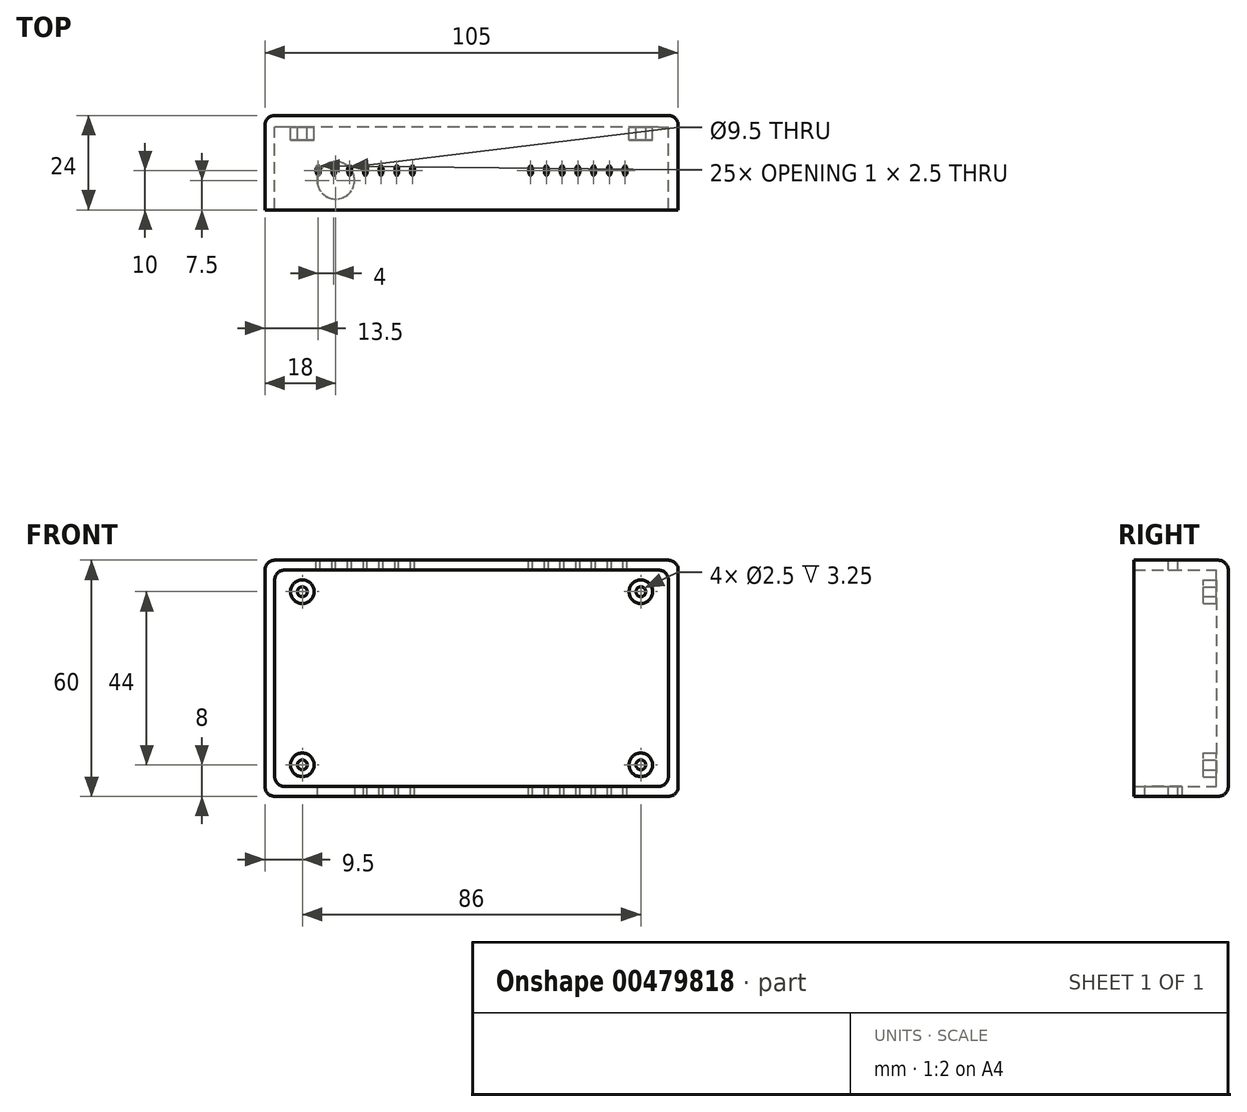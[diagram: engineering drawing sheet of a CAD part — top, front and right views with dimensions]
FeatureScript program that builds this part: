
annotation { "Feature Type Name" : "Feature", "Feature Type Description" : "" }
export const myFeature = defineFeature(function(context is Context, id is Id, definition is map)
    precondition{}
    {
        {
            var Q0;
            Q0=qCreatedBy(makeId("Front.planeOp"),FACE);
            var sketch = newSketch(context, id + "F0", { "sketchPlane" : qUnion([Q0])});
            skLineSegment(sketch, "E0.bottom", {"start": v(50, 27.5) * mm, "end": v(-50, 27.5) * mm});
            skLineSegment(sketch, "E0.top", {"start": v(50, -27.5) * mm, "end": v(-50, -27.5) * mm});
            skLineSegment(sketch, "E0.left", {"start": v(50, 27.5) * mm, "end": v(50, -27.5) * mm});
            skLineSegment(sketch, "E0.right", {"start": v(-50, 27.5) * mm, "end": v(-50, -27.5) * mm});
            skPoint(sketch, "E0.middle", {"position": v(0, 0) * mm});
            skLineSegment(sketch, "E1.bottom", {"start": v(-52.5, 30) * mm, "end": v(52.5, 30) * mm});
            skLineSegment(sketch, "E1.top", {"start": v(-52.5, -30) * mm, "end": v(52.5, -30) * mm});
            skLineSegment(sketch, "E1.left", {"start": v(-52.5, 30) * mm, "end": v(-52.5, -30) * mm});
            skLineSegment(sketch, "E1.right", {"start": v(52.5, 30) * mm, "end": v(52.5, -30) * mm});
            skSolve(sketch);
        }
        {
            var Q0;
            Q0=makeQuery(id+"F0.imprint","IMPRINT",FACE,{"disambiguationData":[TD([[makeQuery(id+"F0.imprint","IMPRINT",EDGE,{"derivedFrom":sQuery(id+"F0.wireOp",EDGE,"E0.bottom")}),1.0]])]});
            var sketch = newSketch(context, id + "F1", { "sketchPlane" : qUnion([Q0])});
            skLineSegment(sketch, "E2.bottom", {"start": v(-43, -22) * mm, "end": v(43, -22) * mm, "construction": true});
            skLineSegment(sketch, "E2.top", {"start": v(-43, 22) * mm, "end": v(43, 22) * mm, "construction": true});
            skLineSegment(sketch, "E2.left", {"start": v(-43, -22) * mm, "end": v(-43, 22) * mm, "construction": true});
            skLineSegment(sketch, "E2.right", {"start": v(43, -22) * mm, "end": v(43, 22) * mm, "construction": true});
            skPoint(sketch, "E2.middle", {"position": v(0, 0) * mm});
            skCircle(sketch, "E3", {"center": v(-43, 22) * mm, "radius": 1.25 * mm});
            skCircle(sketch, "E4", {"center": v(-43, 22) * mm, "radius": 3 * mm});
            skCircle(sketch, "E5", {"center": v(-43, -22) * mm, "radius": 1.25 * mm});
            skCircle(sketch, "E6", {"center": v(-43, -22) * mm, "radius": 3 * mm});
            skCircle(sketch, "E7", {"center": v(43, -22) * mm, "radius": 1.25 * mm});
            skCircle(sketch, "E8", {"center": v(43, -22) * mm, "radius": 3 * mm});
            skCircle(sketch, "E9", {"center": v(43, 22) * mm, "radius": 1.25 * mm});
            skCircle(sketch, "E10", {"center": v(43, 22) * mm, "radius": 3 * mm});
            skLineSegment(sketch, "E11.bottom", {"start": v(-43, -22) * mm, "end": v(-34.5, -22) * mm, "construction": true});
            skLineSegment(sketch, "E11.top", {"start": v(-43, -31.16) * mm, "end": v(-34.5, -31.16) * mm, "construction": true});
            skLineSegment(sketch, "E11.left", {"start": v(-43, -22) * mm, "end": v(-43, -31.16) * mm, "construction": true});
            skLineSegment(sketch, "E11.right", {"start": v(-34.5, -22) * mm, "end": v(-34.5, -31.16) * mm, "construction": true});
            skSolve(sketch);
        }
        {
            var Q0;
            Q0=makeQuery(id+"F0.imprint","IMPRINT",FACE,{"disambiguationData":[TD([[makeQuery(id+"F0.imprint","IMPRINT",EDGE,{"derivedFrom":sQuery(id+"F0.wireOp",EDGE,"E0.bottom")}),-1.0]])]});
            extrude(context, id + "F2", {"entities" : qUnion([Q0]), "depth" : 24 * mm});
        }
        {
            var Q0;
            Q0=makeQuery(id+"F0.imprint","IMPRINT",FACE,{"disambiguationData":[TD([[makeQuery(id+"F0.imprint","IMPRINT",EDGE,{"derivedFrom":sQuery(id+"F0.wireOp",EDGE,"E0.bottom")}),1.0]])]});
            var Q1;
            Q1=makeQuery(id+"F1.imprint","IMPRINT",FACE,{"disambiguationData":[TD([[makeQuery(id+"F1.imprint","IMPRINT",EDGE,{"derivedFrom":sQuery(id+"F1.wireOp",EDGE,"E9")}),-1.0]])]});
            var Q2;
            Q2=makeQuery(id+"F1.imprint","IMPRINT",FACE,{"disambiguationData":[TD([[makeQuery(id+"F1.imprint","IMPRINT",EDGE,{"derivedFrom":sQuery(id+"F1.wireOp",EDGE,"E4")}),-1.0]])]});
            extrude(context, id + "F3", {"entities" : qUnion([Q0, Q1, Q2]), "operationType" : NewBodyOperationType.ADD, "depth" : 3 * mm});
        }
        {
            var Q0;
            Q0=makeQuery(id+"F2.opExtrude","CAP_EDGE",EDGE,{"disambiguationData":[OSD([sQuery(id+"F0.wireOp",EDGE,"E1.top")])],"isStart":true});
            var Q1;
            Q1=makeQuery(id+"F2.opExtrude","CAP_EDGE",EDGE,{"disambiguationData":[OSD([sQuery(id+"F0.wireOp",EDGE,"E1.bottom")])],"isStart":true});
            var Q2;
            Q2=makeQuery(id+"F2.opExtrude","CAP_EDGE",EDGE,{"disambiguationData":[OSD([sQuery(id+"F0.wireOp",EDGE,"E1.left")])],"isStart":true});
            var Q3;
            Q3=makeQuery(id+"F2.opExtrude","CAP_EDGE",EDGE,{"disambiguationData":[OSD([sQuery(id+"F0.wireOp",EDGE,"E1.right")])],"isStart":true});
            fillet(context, id + "F4", {"entities" : qUnion([Q0, Q1, Q2, Q3]), "radius" : 2.5 * mm, "tangentPropagation" : true, "allowEdgeOverflow" : false});
        }
        {
            var Q0;
            Q0=makeQuery(id+"F2.opExtrude","SWEPT_EDGE",EDGE,{"disambiguationData":[OSD([sQuery(id+"F0.wireOp",EDGE,"E1.bottom"),sQuery(id+"F0.wireOp",EDGE,"E1.left")])]});
            var Q1;
            Q1=makeQuery(id+"F2.opExtrude","SWEPT_EDGE",EDGE,{"disambiguationData":[OSD([sQuery(id+"F0.wireOp",EDGE,"E1.bottom"),sQuery(id+"F0.wireOp",EDGE,"E1.right")])]});
            var Q2;
            Q2=makeQuery(id+"F2.opExtrude","SWEPT_EDGE",EDGE,{"disambiguationData":[OSD([sQuery(id+"F0.wireOp",EDGE,"E1.top"),sQuery(id+"F0.wireOp",EDGE,"E1.right")])]});
            var Q3;
            Q3=makeQuery(id+"F2.opExtrude","SWEPT_EDGE",EDGE,{"disambiguationData":[OSD([sQuery(id+"F0.wireOp",EDGE,"E1.top"),sQuery(id+"F0.wireOp",EDGE,"E1.left")])]});
            fillet(context, id + "F5", {"entities" : qUnion([Q0, Q1, Q2, Q3]), "radius" : 2.5 * mm, "tangentPropagation" : true, "allowEdgeOverflow" : false});
        }
        {
            var Q0;
            Q0=makeQuery(id+"F2.opExtrude","SWEPT_EDGE",EDGE,{"disambiguationData":[OSD([sQuery(id+"F0.wireOp",EDGE,"E0.top"),sQuery(id+"F0.wireOp",EDGE,"E0.right")])]});
            var Q1;
            Q1=makeQuery(id+"F2.opExtrude","SWEPT_EDGE",EDGE,{"disambiguationData":[OSD([sQuery(id+"F0.wireOp",EDGE,"E0.bottom"),sQuery(id+"F0.wireOp",EDGE,"E0.right")])]});
            var Q2;
            Q2=makeQuery(id+"F2.opExtrude","SWEPT_EDGE",EDGE,{"disambiguationData":[OSD([sQuery(id+"F0.wireOp",EDGE,"E0.bottom"),sQuery(id+"F0.wireOp",EDGE,"E0.left")])]});
            var Q3;
            Q3=makeQuery(id+"F2.opExtrude","SWEPT_EDGE",EDGE,{"disambiguationData":[OSD([sQuery(id+"F0.wireOp",EDGE,"E0.top"),sQuery(id+"F0.wireOp",EDGE,"E0.left")])]});
            fillet(context, id + "F6", {"entities" : qUnion([Q0, Q1, Q2, Q3]), "radius" : 2.5 * mm, "tangentPropagation" : true, "allowEdgeOverflow" : false});
        }
        {
            var Q0;
            Q0=qSketchRegion(id+"F1",true);
            extrude(context, id + "F7", {"entities" : qUnion([Q0]), "operationType" : NewBodyOperationType.ADD, "depth" : 6.25 * mm});
        }
        {
            var Q0;
            Q0=makeQuery(id+"F2.opExtrude","SWEPT_FACE",FACE,{"disambiguationData":[OSD([sQuery(id+"F0.wireOp",EDGE,"E1.bottom")])]});
            var sketch = newSketch(context, id + "F8", { "sketchPlane" : qUnion([Q0])});
            skLineSegment(sketch, "E12", {"start": v(0, 0) * mm, "end": v(0, -12) * mm});
            skEllipse(sketch, "E13", {"center": v(-39, -14) * mm, "majorRadius": 0.5 * mm, "minorRadius": 1.25 * mm, "majorAxis": v(-1, 0)});
            skEllipse(sketch, "E14", {"center": v(39, -14) * mm, "majorRadius": 0.5 * mm, "minorRadius": 1.25 * mm, "majorAxis": v(-1, 0)});
            skEllipse(sketch, "E15", {"center": v(-35, -14) * mm, "majorRadius": 0.5 * mm, "minorRadius": 1.25 * mm, "majorAxis": v(-1, 0)});
            skEllipse(sketch, "E16", {"center": v(-31, -14) * mm, "majorRadius": 0.5 * mm, "minorRadius": 1.25 * mm, "majorAxis": v(-1, 0)});
            skEllipse(sketch, "E17", {"center": v(27, -14) * mm, "majorRadius": 0.5 * mm, "minorRadius": 1.25 * mm, "majorAxis": v(-1, 0)});
            skEllipse(sketch, "E18", {"center": v(23, -14) * mm, "majorRadius": 0.5 * mm, "minorRadius": 1.25 * mm, "majorAxis": v(-1, 0)});
            skEllipse(sketch, "E19", {"center": v(19, -14) * mm, "majorRadius": 0.5 * mm, "minorRadius": 1.25 * mm, "majorAxis": v(-1, 0)});
            skEllipse(sketch, "E20", {"center": v(15, -14) * mm, "majorRadius": 0.5 * mm, "minorRadius": 1.25 * mm, "majorAxis": v(-1, 0)});
            skEllipse(sketch, "E21", {"center": v(-27, -14) * mm, "majorRadius": 0.5 * mm, "minorRadius": 1.25 * mm, "majorAxis": v(-1, 0)});
            skEllipse(sketch, "E22", {"center": v(-19, -14) * mm, "majorRadius": 0.5 * mm, "minorRadius": 1.25 * mm, "majorAxis": v(-1, 0)});
            skEllipse(sketch, "E23", {"center": v(-15, -14) * mm, "majorRadius": 0.5 * mm, "minorRadius": 1.25 * mm, "majorAxis": v(-1, 0)});
            skEllipse(sketch, "E24", {"center": v(31, -14) * mm, "majorRadius": 0.5 * mm, "minorRadius": 1.25 * mm, "majorAxis": v(-1, 0)});
            skEllipse(sketch, "E25", {"center": v(35, -14) * mm, "majorRadius": 0.5 * mm, "minorRadius": 1.25 * mm, "majorAxis": v(-1, 0)});
            skEllipse(sketch, "E26", {"center": v(-23, -14) * mm, "majorRadius": 0.5 * mm, "minorRadius": 1.25 * mm, "majorAxis": v(-1, 0)});
            skSolve(sketch);
        }
        {
            var Q0;
            Q0=makeQuery(id+"F8.imprint","IMPRINT",FACE,{"disambiguationData":[TD([[makeQuery(id+"F8.imprint","IMPRINT",EDGE,{"derivedFrom":sQuery(id+"F8.wireOp",EDGE,"E20")}),1.0]])]});
            var Q1;
            Q1=makeQuery(id+"F8.imprint","IMPRINT",FACE,{"disambiguationData":[TD([[makeQuery(id+"F8.imprint","IMPRINT",EDGE,{"derivedFrom":sQuery(id+"F8.wireOp",EDGE,"E19")}),1.0]])]});
            var Q2;
            Q2=makeQuery(id+"F8.imprint","IMPRINT",FACE,{"disambiguationData":[TD([[makeQuery(id+"F8.imprint","IMPRINT",EDGE,{"derivedFrom":sQuery(id+"F8.wireOp",EDGE,"E18")}),1.0]])]});
            var Q3;
            Q3=makeQuery(id+"F8.imprint","IMPRINT",FACE,{"disambiguationData":[TD([[makeQuery(id+"F8.imprint","IMPRINT",EDGE,{"derivedFrom":sQuery(id+"F8.wireOp",EDGE,"E17")}),1.0]])]});
            var Q4;
            Q4=makeQuery(id+"F8.imprint","IMPRINT",FACE,{"disambiguationData":[TD([[makeQuery(id+"F8.imprint","IMPRINT",EDGE,{"derivedFrom":sQuery(id+"F8.wireOp",EDGE,"E24")}),1.0]])]});
            var Q5;
            Q5=makeQuery(id+"F8.imprint","IMPRINT",FACE,{"disambiguationData":[TD([[makeQuery(id+"F8.imprint","IMPRINT",EDGE,{"derivedFrom":sQuery(id+"F8.wireOp",EDGE,"E25")}),1.0]])]});
            var Q6;
            Q6=makeQuery(id+"F8.imprint","IMPRINT",FACE,{"disambiguationData":[TD([[makeQuery(id+"F8.imprint","IMPRINT",EDGE,{"derivedFrom":sQuery(id+"F8.wireOp",EDGE,"E14")}),1.0]])]});
            var Q7;
            Q7=makeQuery(id+"F8.imprint","IMPRINT",FACE,{"disambiguationData":[TD([[makeQuery(id+"F8.imprint","IMPRINT",EDGE,{"derivedFrom":sQuery(id+"F8.wireOp",EDGE,"E23")}),1.0]])]});
            var Q8;
            Q8=makeQuery(id+"F8.imprint","IMPRINT",FACE,{"disambiguationData":[TD([[makeQuery(id+"F8.imprint","IMPRINT",EDGE,{"derivedFrom":sQuery(id+"F8.wireOp",EDGE,"E22")}),1.0]])]});
            var Q9;
            Q9=makeQuery(id+"F8.imprint","IMPRINT",FACE,{"disambiguationData":[TD([[makeQuery(id+"F8.imprint","IMPRINT",EDGE,{"derivedFrom":sQuery(id+"F8.wireOp",EDGE,"E26")}),1.0]])]});
            var Q10;
            Q10=makeQuery(id+"F8.imprint","IMPRINT",FACE,{"disambiguationData":[TD([[makeQuery(id+"F8.imprint","IMPRINT",EDGE,{"derivedFrom":sQuery(id+"F8.wireOp",EDGE,"E21")}),1.0]])]});
            var Q11;
            Q11=sQuery(id+"F8.wireOp",EDGE,"E20");
            extrude(context, id + "F9", {"entities" : qUnion([Q0, Q1, Q2, Q3, Q4, Q5, Q6, Q7, Q8, Q9, Q10]), "operationType" : NewBodyOperationType.REMOVE, "surfaceEntities" : qUnion([Q11]), "endBound" : BoundingType.THROUGH_ALL, "oppositeDirection" : true, "depth" : 25 * mm});
        }
        {
            var Q0;
            Q0=makeQuery(id+"F2.opExtrude","SWEPT_FACE",FACE,{"disambiguationData":[OSD([sQuery(id+"F0.wireOp",EDGE,"E1.top")])]});
            var sketch = newSketch(context, id + "F10", { "sketchPlane" : qUnion([Q0])});
            skLineSegment(sketch, "E27", {"start": v(-34.5, 0) * mm, "end": v(-34.5, 16.5) * mm, "construction": true});
            skCircle(sketch, "E28", {"center": v(-34.5, 16.5) * mm, "radius": 4.75 * mm});
            skSolve(sketch);
        }
        {
            var Q0;
            Q0=makeQuery(id+"F8.imprint","IMPRINT",FACE,{"disambiguationData":[TD([[makeQuery(id+"F8.imprint","IMPRINT",EDGE,{"derivedFrom":sQuery(id+"F8.wireOp",EDGE,"E16")}),1.0]])]});
            var Q1;
            Q1=makeQuery(id+"F8.imprint","IMPRINT",FACE,{"disambiguationData":[TD([[makeQuery(id+"F8.imprint","IMPRINT",EDGE,{"derivedFrom":sQuery(id+"F8.wireOp",EDGE,"E15")}),1.0]])]});
            var Q2;
            Q2=makeQuery(id+"F8.imprint","IMPRINT",FACE,{"disambiguationData":[TD([[makeQuery(id+"F8.imprint","IMPRINT",EDGE,{"derivedFrom":sQuery(id+"F8.wireOp",EDGE,"E13")}),1.0]])]});
            extrude(context, id + "F11", {"entities" : qUnion([Q0, Q1, Q2]), "operationType" : NewBodyOperationType.REMOVE, "oppositeDirection" : true, "depth" : 25 * mm, "hasSecondDirection" : true, "secondDirectionOppositeDirection" : false, "secondDirectionDepth" : 10 * mm});
        }
        {
            var Q0;
            Q0=makeQuery(id+"F10.imprint","IMPRINT",FACE,{"disambiguationData":[TD([[makeQuery(id+"F10.imprint","IMPRINT",EDGE,{"derivedFrom":sQuery(id+"F10.wireOp",EDGE,"E28")}),1.0]])]});
            extrude(context, id + "F12", {"entities" : qUnion([Q0]), "operationType" : NewBodyOperationType.REMOVE, "oppositeDirection" : true, "depth" : 10 * mm});
        }
    });
